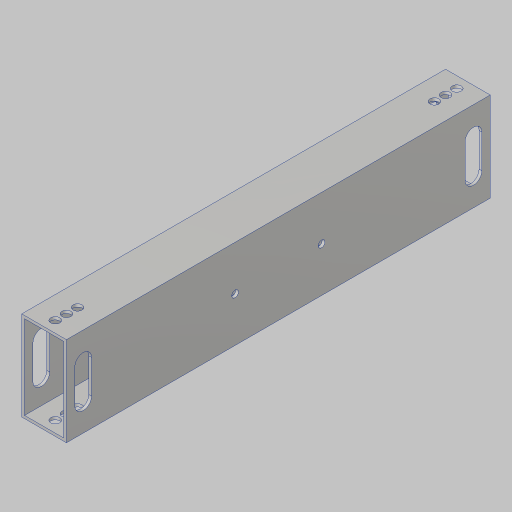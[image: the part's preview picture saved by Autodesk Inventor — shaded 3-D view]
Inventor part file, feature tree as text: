
AUTODESK INVENTOR PART (.ipt)
format: ipt  version: 2023.5 (Build 275446000, 446)  size: 162,816 bytes
history: native  units: in
note: dims shown in document units (in); Inventor stores cm internally (conversion verified against a paired STEP export)
features: sketch x3, extrude x2, hole x2
ambient origin geometry x8: Origin, YZ Plane, XZ Plane, XY Plane, X Axis, Y Axis, Z Axis, Center Point
bodies: Solid1 (feature_tree)
feature tree (7):
  extrude  "Extrusion1"  Depth=0.25in
  hole  "Hole2"  [1 undecoded]
  extrude  "Extrusion2"  Depth=1.0in
  hole  "Hole3"  [1 undecoded]
  sketch  "Sketch3"  dims[d4=0.0in d18=0.25in]
  sketch  "Sketch4"  dims[d19=0.25in d20=0.25in]
  sketch  "Sketch5"  dims[d21=0.5in d22=0.25in d23=0.25in d24=0.25in d25=0.201in d26=0.75in d27=0.385in d28=0.25in d29=0.5635in d30=1.0in d31=0.8108in d32=0.375in d33=0.75in d34=0.375in d35=0.0in d36=0.0in d37=1.9366in d38=0.15in d39=0.75in d40=0.279in d41=0.25in d42=0.5635in d43=1.0in d44=0.8108in]
note: 2 required parameter values undecoded (feature->parameter linkage not recoverable at this tier; creation-order binding heuristic only, values carry confidence <= 0.55)
